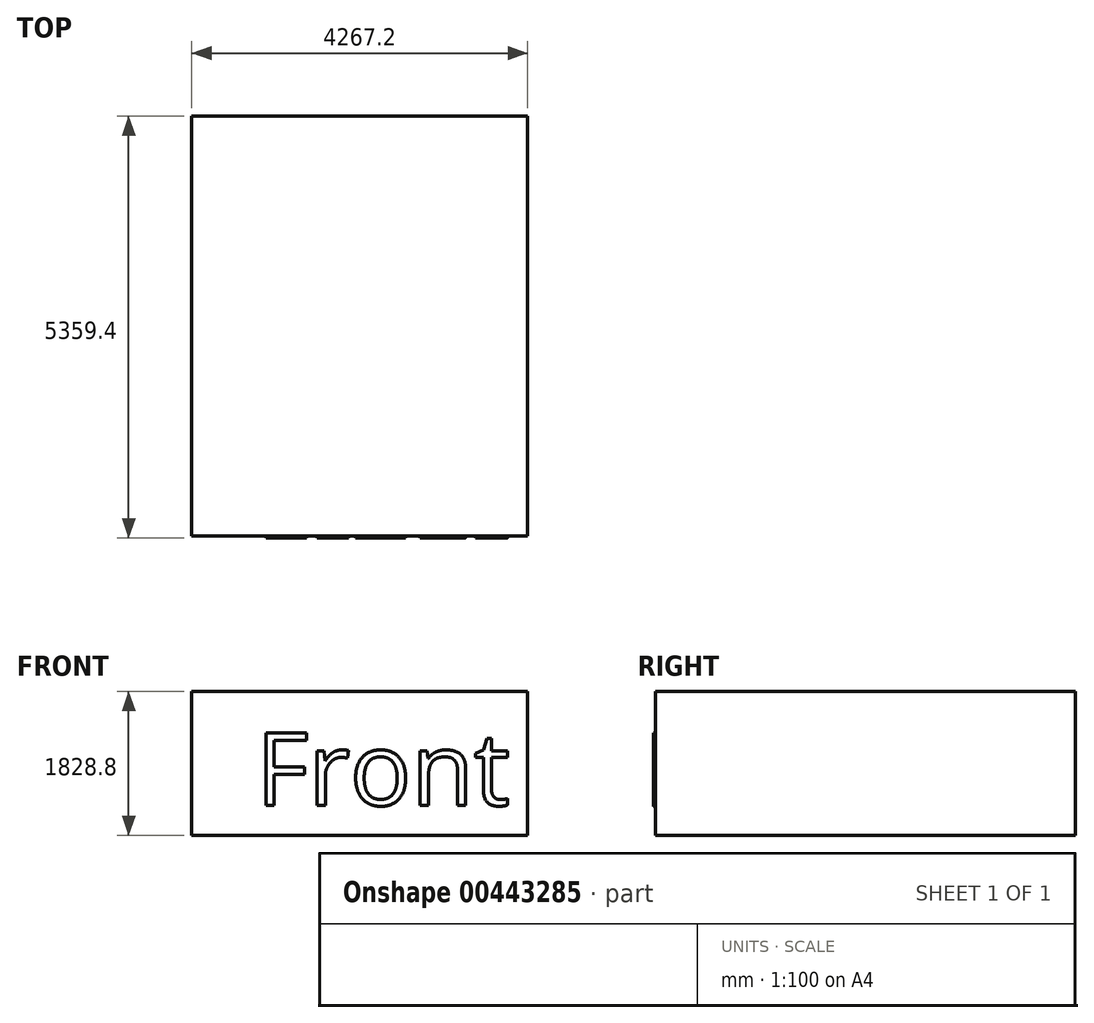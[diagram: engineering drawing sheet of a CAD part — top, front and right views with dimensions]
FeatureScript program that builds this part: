
annotation { "Feature Type Name" : "Feature", "Feature Type Description" : "" }
export const myFeature = defineFeature(function(context is Context, id is Id, definition is map)
    precondition{}
    {
        {
            var Q0;
            Q0=qCreatedBy(makeId("Top.planeOp"),FACE);
            var sketch = newSketch(context, id + "F0", { "sketchPlane" : qUnion([Q0])});
            skLineSegment(sketch, "E0.bottom", {"start": v(2133.6, 2667) * mm, "end": v(-2133.6, 2667) * mm});
            skLineSegment(sketch, "E0.top", {"start": v(2133.6, -2667) * mm, "end": v(-2133.6, -2667) * mm});
            skLineSegment(sketch, "E0.left", {"start": v(2133.6, 2667) * mm, "end": v(2133.6, -2667) * mm});
            skLineSegment(sketch, "E0.right", {"start": v(-2133.6, 2667) * mm, "end": v(-2133.6, -2667) * mm});
            skPoint(sketch, "E0.middle", {"position": v(0, 0) * mm});
            skSolve(sketch);
        }
        {
            var Q0;
            Q0 = qSketchRegion(id + "F0", true);
            extrude(context, id + "F1", {"entities" : qUnion([Q0]), "depth" : 1828.8 * mm});
        }
        {
            var Q0;
            Q0=makeQuery(id+"F1.opExtrude","SWEPT_FACE",FACE,{"disambiguationData":[OSD([sQuery(id+"F0.wireOp",EDGE,"E0.top")])]});
            var sketch = newSketch(context, id + "F2", { "sketchPlane" : qUnion([Q0])});
            skText(sketch, "E1", { "text": "Front\n", "fontName": "OpenSans-Regular.ttf"});
            const initialGuessF2  = {"E1": [-1.32063, 0.38178, 1, 0, 0.93127]};
            skSetInitialGuess(sketch, initialGuessF2);
            skSolve(sketch);
        }
        {
            var Q0;
            Q0 = qSketchRegion(id + "F2", true);
            extrude(context, id + "F3", {"entities" : qUnion([Q0]), "operationType" : NewBodyOperationType.ADD, "depth" : 25.4 * mm});
        }
    });
